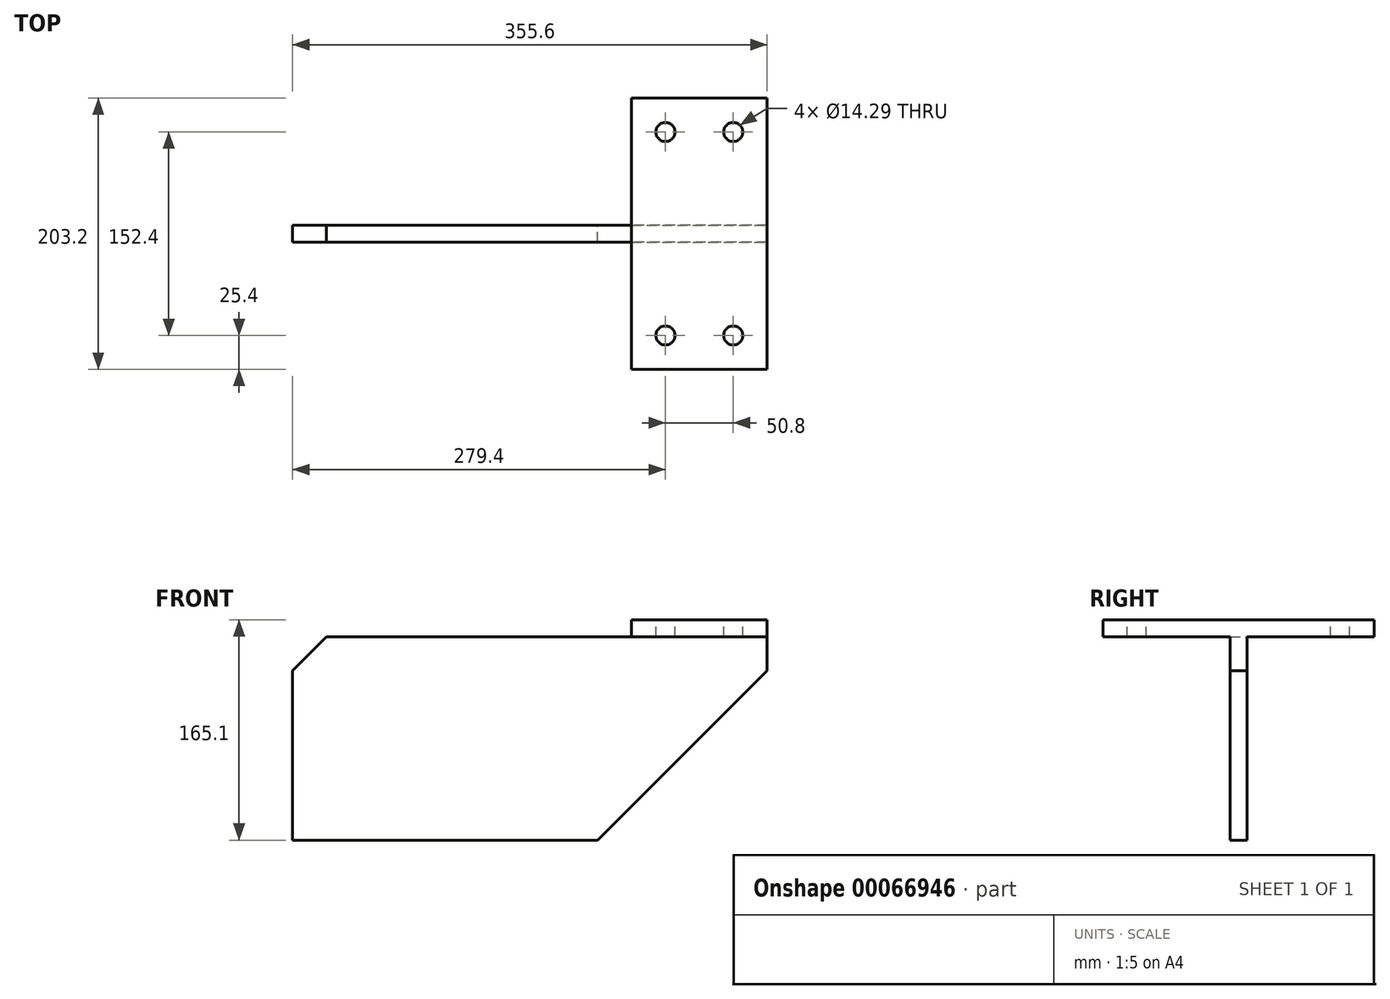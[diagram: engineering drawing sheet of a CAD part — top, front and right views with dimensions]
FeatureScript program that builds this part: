
annotation { "Feature Type Name" : "Feature", "Feature Type Description" : "" }
export const myFeature = defineFeature(function(context is Context, id is Id, definition is map)
    precondition{}
    {
        {
            var Q0;
            Q0=qCreatedBy(makeId("Front.planeOp"),FACE);
            var sketch = newSketch(context, id + "F0", { "sketchPlane" : qUnion([Q0])});
            skLineSegment(sketch, "E0.bottom", {"start": v(0, 0) * mm, "end": v(101.6, 0) * mm});
            skLineSegment(sketch, "E0.top", {"start": v(0, 12.7) * mm, "end": v(101.6, 12.7) * mm});
            skLineSegment(sketch, "E0.left", {"start": v(0, 0) * mm, "end": v(0, 12.7) * mm});
            skLineSegment(sketch, "E0.right", {"start": v(101.6, 0) * mm, "end": v(101.6, 12.7) * mm});
            skLineSegment(sketch, "E1.bottom", {"start": v(101.6, 0) * mm, "end": v(-228.6, 0) * mm});
            skLineSegment(sketch, "E1.top", {"start": v(-25.4, -152.4) * mm, "end": v(-254, -152.4) * mm});
            skLineSegment(sketch, "E1.left", {"start": v(101.6, 0) * mm, "end": v(101.6, -25.4) * mm});
            skLineSegment(sketch, "E1.right", {"start": v(-254, -25.4) * mm, "end": v(-254, -152.4) * mm});
            skLineSegment(sketch, "E2", {"start": v(101.6, -25.4) * mm, "end": v(-25.4, -152.4) * mm});
            skLineSegment(sketch, "E3", {"start": v(-228.6, 0) * mm, "end": v(-254, -25.4) * mm});
            skPoint(sketch, "E4.orphan", {"position": v(-254, 0) * mm});
            skSolve(sketch);
        }
        {
            var Q0;
            Q0=makeQuery(id+"F0.imprint","IMPRINT",FACE,{"disambiguationData":[TD([[makeQuery(id+"F0.imprint","IMPRINT",EDGE,{"derivedFrom":sQuery(id+"F0.wireOp",EDGE,"E1.top")}),-1.0]])]});
            extrude(context, id + "F1", {"entities" : qUnion([Q0]), "endBound" : BoundingType.SYMMETRIC, "depth" : 12.7 * mm});
        }
        {
            var Q0;
            Q0=makeQuery(id+"F0.imprint","IMPRINT",FACE,{"disambiguationData":[TD([[makeQuery(id+"F0.imprint","IMPRINT",EDGE,{"derivedFrom":sQuery(id+"F0.wireOp",EDGE,"E0.top")}),-1.0]])]});
            extrude(context, id + "F2", {"entities" : qUnion([Q0]), "operationType" : NewBodyOperationType.ADD, "endBound" : BoundingType.SYMMETRIC, "depth" : 203.2 * mm});
        }
        {
            var Q0;
            Q0=makeQuery(id+"F2.opExtrude","SWEPT_FACE",FACE,{"disambiguationData":[OSD([sQuery(id+"F0.wireOp",EDGE,"E0.top")])]});
            var sketch = newSketch(context, id + "F3", { "sketchPlane" : qUnion([Q0])});
            skLineSegment(sketch, "E5", {"start": v(50.8, 101.6) * mm, "end": v(50.8, -101.6) * mm, "construction": true});
            skLineSegment(sketch, "E6", {"start": v(101.6, 0) * mm, "end": v(-285.57, 0) * mm, "construction": true});
            skPoint(sketch, "E6.endSnap0", {"position": v(50.8, 0) * mm});
            skLineSegment(sketch, "E7.0", {"start": v(25.4, 101.6) * mm, "end": v(25.4, -101.6) * mm, "construction": true});
            skLineSegment(sketch, "E8.0", {"start": v(101.6, 76.2) * mm, "end": v(-285.57, 76.2) * mm, "construction": true});
            skPoint(sketch, "E9", {"position": v(25.4, 76.2) * mm});
            skPoint(sketch, "E10.0.1.0", {"position": v(25.4, -76.2) * mm});
            skPoint(sketch, "E10.1.0.0", {"position": v(76.2, 76.2) * mm});
            skPoint(sketch, "E10.1.1.0", {"position": v(76.2, -76.2) * mm});
            skLineSegment(sketch, "E10.direction1", {"start": v(25.4, 76.2) * mm, "end": v(76.2, 76.2) * mm, "construction": true});
            skLineSegment(sketch, "E10.direction2", {"start": v(25.4, 76.2) * mm, "end": v(25.4, -76.2) * mm, "construction": true});
            skSolve(sketch);
        }
        {
            var Q0;
            Q0=sQuery(id+"F3.wireOp",VERTEX,"E9");
            var Q1;
            Q1=sQuery(id+"F3.wireOp",VERTEX,"E10.1.0.0");
            var Q2;
            Q2=sQuery(id+"F3.wireOp",VERTEX,"E10.1.1.0");
            var Q3;
            Q3=sQuery(id+"F3.wireOp",VERTEX,"E10.0.1.0");
            var Q4;
            Q4=makeQuery(id+"F1.opExtrude","SWEPT_BODY",BODY,{"disambiguationData":[OSD([sQuery(id+"F0.wireOp",EDGE,"E1.bottom"),sQuery(id+"F0.wireOp",EDGE,"E1.top"),sQuery(id+"F0.wireOp",EDGE,"E1.left"),sQuery(id+"F0.wireOp",EDGE,"E1.right"),sQuery(id+"F0.wireOp",EDGE,"E2"),sQuery(id+"F0.wireOp",EDGE,"E3")])]});
            hole(context, id + "F4", {"style" : HoleStyle.SIMPLE, "holeDiameter" : 14.29 * mm, "endStyle" : HoleEndStyle.THROUGH, "locations" : qUnion([Q0, Q1, Q2, Q3]), "scope" : qUnion([Q4])});
        }
    });
